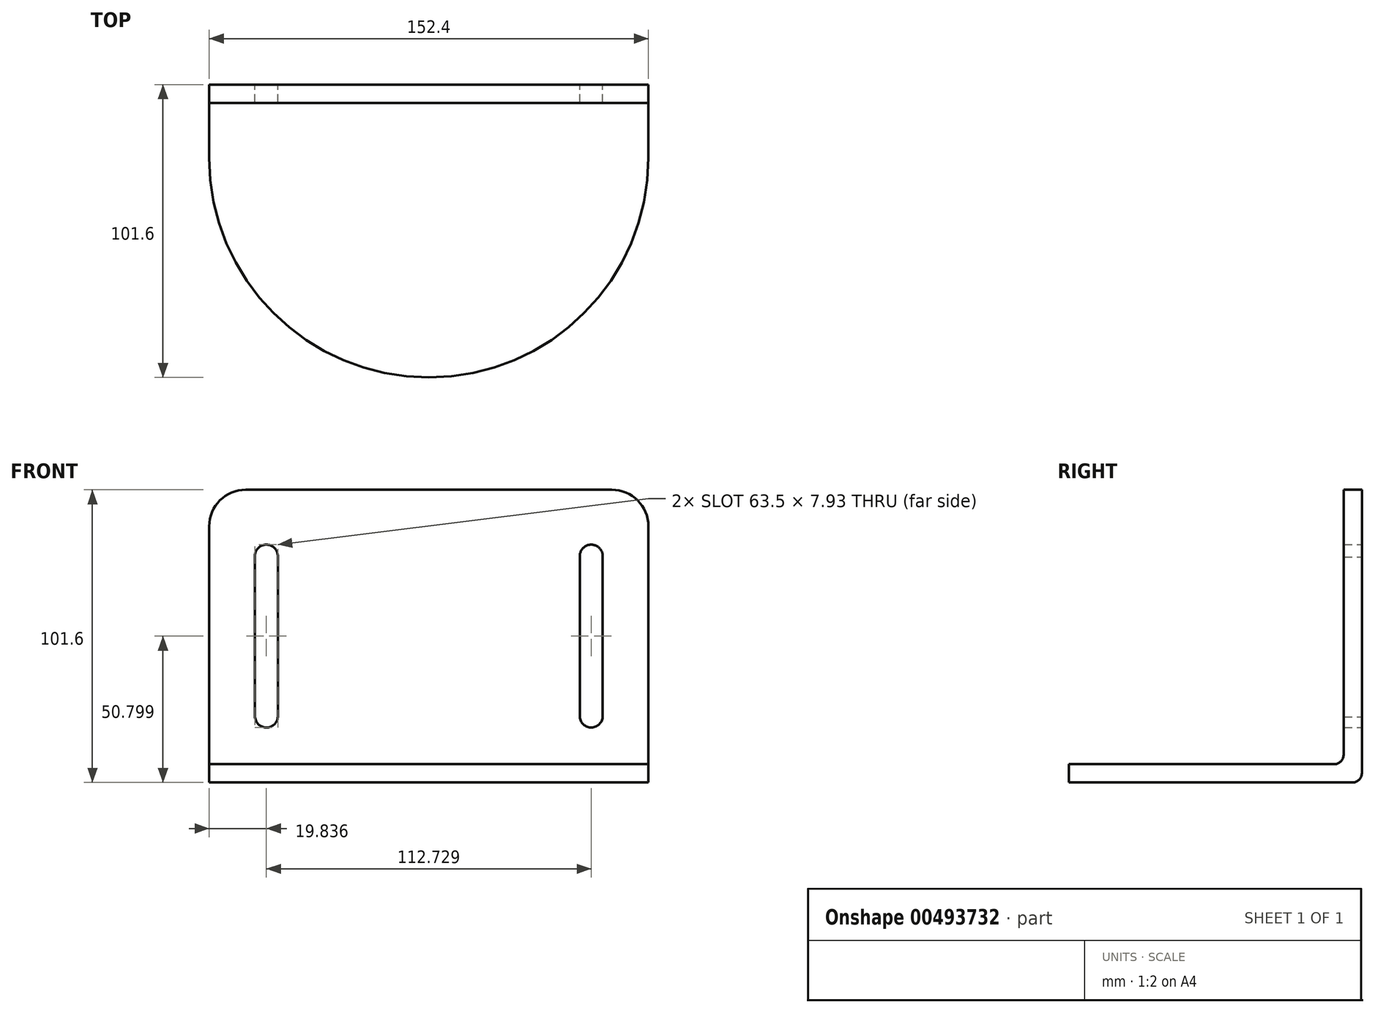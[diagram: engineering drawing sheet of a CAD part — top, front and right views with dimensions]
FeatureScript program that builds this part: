
annotation { "Feature Type Name" : "Feature", "Feature Type Description" : "" }
export const myFeature = defineFeature(function(context is Context, id is Id, definition is map)
    precondition{}
    {
        {
            var Q0;
            Q0=qCreatedBy(makeId("Front.planeOp"),FACE);
            var sketch = newSketch(context, id + "F0", { "sketchPlane" : qUnion([Q0])});
            skLineSegment(sketch, "E0.bottom", {"start": v(0, 0) * mm, "end": v(152.4, 0) * mm});
            skLineSegment(sketch, "E0.top", {"start": v(12.7, 101.6) * mm, "end": v(139.7, 101.6) * mm});
            skLineSegment(sketch, "E0.left", {"start": v(0, 0) * mm, "end": v(0, 88.9) * mm});
            skLineSegment(sketch, "E0.right", {"start": v(152.4, 0) * mm, "end": v(152.4, 88.9) * mm});
            skLineSegment(sketch, "E1", {"start": v(76.2, 101.6) * mm, "end": v(76.2, 0) * mm, "construction": true});
            skArc(sketch, "E2", {"start": v(23.8, 78.58) * mm, "mid": v(19.68, 82.55) * mm, "end": v(15.87, 78.28) * mm});
            skArc(sketch, "E3", {"start": v(15.87, 23.02) * mm, "mid": v(19.72, 19.05) * mm, "end": v(23.8, 22.78) * mm});
            skLineSegment(sketch, "E4", {"start": v(15.87, 78.28) * mm, "end": v(15.87, 23.02) * mm});
            skLineSegment(sketch, "E5", {"start": v(23.8, 78.58) * mm, "end": v(23.8, 22.78) * mm});
            skLineSegment(sketch, "E6.MirrorCS", {"start": v(128.6, 78.58) * mm, "end": v(128.6, 22.78) * mm});
            skArc(sketch, "E7.MirrorCS", {"start": v(128.6, 78.58) * mm, "mid": v(132.72, 82.55) * mm, "end": v(136.52, 78.28) * mm});
            skLineSegment(sketch, "E8.MirrorCS", {"start": v(136.52, 78.28) * mm, "end": v(136.53, 23.02) * mm});
            skArc(sketch, "E9.MirrorCS", {"start": v(136.53, 23.02) * mm, "mid": v(132.68, 19.05) * mm, "end": v(128.6, 22.78) * mm});
            skPoint(sketch, "E10.visualSharp", {"position": v(0, 101.6) * mm});
            skArc(sketch, "E10.filletArc", {"start": v(12.7, 101.6) * mm, "mid": v(3.72, 97.88) * mm, "end": v(0, 88.9) * mm});
            skPoint(sketch, "E11.visualSharp", {"position": v(152.4, 101.6) * mm});
            skArc(sketch, "E11.filletArc", {"start": v(152.4, 88.9) * mm, "mid": v(148.68, 97.88) * mm, "end": v(139.7, 101.6) * mm});
            skSolve(sketch);
        }
        {
            var Q0;
            Q0 = qSketchRegion(id + "F0", true);
            extrude(context, id + "F1", {"entities" : qUnion([Q0]), "depth" : 6.35 * mm});
        }
        {
            var Q0;
            Q0=makeQuery(id+"F1.opExtrude","SWEPT_FACE",FACE,{"disambiguationData":[OSD([sQuery(id+"F0.wireOp",EDGE,"E0.bottom")])]});
            var sketch = newSketch(context, id + "F2", { "sketchPlane" : qUnion([Q0])});
            skLineSegment(sketch, "E12", {"start": v(152.4, 0) * mm, "end": v(152.4, 25.4) * mm});
            skPoint(sketch, "E12.endSnap0", {"position": v(152.4, 3.18) * mm});
            skLineSegment(sketch, "E13", {"start": v(0, 0) * mm, "end": v(0, 25.4) * mm});
            skPoint(sketch, "E13.endSnap0", {"position": v(0, 3.18) * mm});
            skArc(sketch, "E14", {"start": v(152.4, 25.4) * mm, "mid": v(76.2, 101.6) * mm, "end": v(0, 25.4) * mm});
            skLineSegment(sketch, "E15", {"start": v(152.4, 0) * mm, "end": v(0, 0) * mm});
            skSolve(sketch);
        }
        {
            var Q0;
            Q0 = qSketchRegion(id + "F2", true);
            extrude(context, id + "F3", {"entities" : qUnion([Q0]), "operationType" : NewBodyOperationType.ADD, "oppositeDirection" : true, "depth" : 6.35 * mm});
        }
        {
            var Q0;
            Q0=makeQuery(id+"F1.opExtrude","CAP_EDGE",EDGE,{"disambiguationData":[OSD([sQuery(id+"F0.wireOp",EDGE,"E0.bottom")])],"isStart":true});
            var Q1;
            Q1=makeQuery(id+"F3.boolean.opBoolean","INTERSECT",EDGE,{"derivedFrom":[makeQuery(id+"F1.opExtrude","CAP_FACE",FACE,{"disambiguationData":[OSD([sQuery(id+"F0.wireOp",EDGE,"E0.bottom"),sQuery(id+"F0.wireOp",EDGE,"E0.top"),sQuery(id+"F0.wireOp",EDGE,"E0.left"),sQuery(id+"F0.wireOp",EDGE,"E0.right"),sQuery(id+"F0.wireOp",EDGE,"E2"),sQuery(id+"F0.wireOp",EDGE,"E3"),sQuery(id+"F0.wireOp",EDGE,"E4"),sQuery(id+"F0.wireOp",EDGE,"E5"),sQuery(id+"F0.wireOp",EDGE,"E6.MirrorCS"),sQuery(id+"F0.wireOp",EDGE,"E7.MirrorCS"),sQuery(id+"F0.wireOp",EDGE,"E8.MirrorCS"),sQuery(id+"F0.wireOp",EDGE,"E9.MirrorCS"),sQuery(id+"F0.wireOp",EDGE,"E10.filletArc"),sQuery(id+"F0.wireOp",EDGE,"E11.filletArc")])],"isStart":false}),makeQuery(id+"F3.opExtrude","CAP_FACE",FACE,{"disambiguationData":[OSD([sQuery(id+"F2.wireOp",EDGE,"E12"),sQuery(id+"F2.wireOp",EDGE,"E13"),sQuery(id+"F2.wireOp",EDGE,"E14"),sQuery(id+"F2.wireOp",EDGE,"E15")])],"isStart":false})]});
            fillet(context, id + "F4", {"entities" : qUnion([Q0, Q1]), "radius" : 3.17 * mm, "tangentPropagation" : true, "allowEdgeOverflow" : false});
        }
    });
